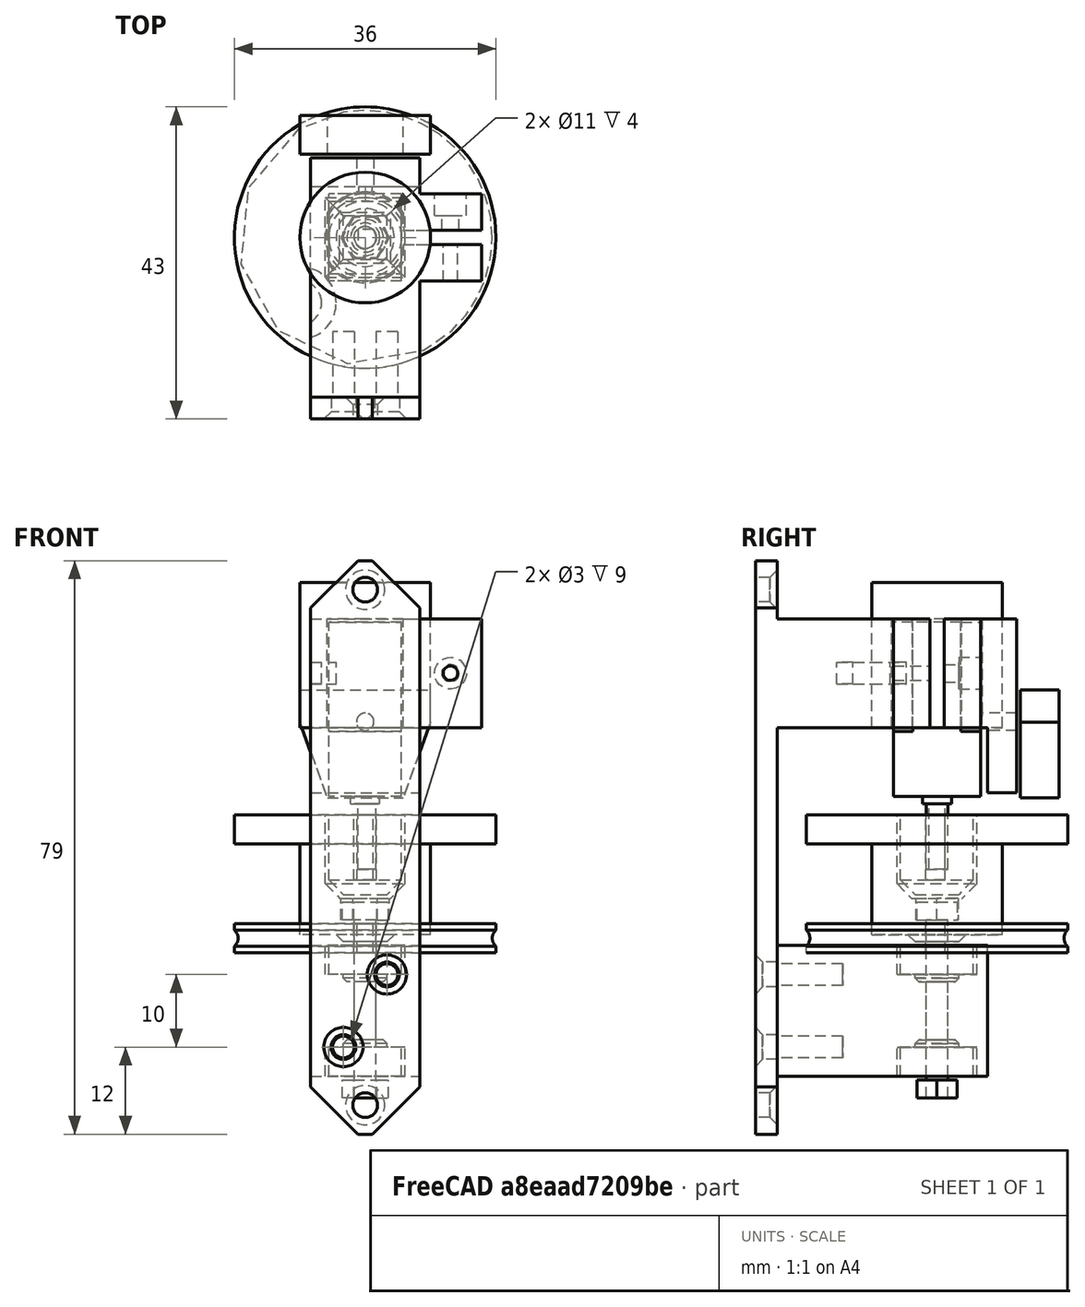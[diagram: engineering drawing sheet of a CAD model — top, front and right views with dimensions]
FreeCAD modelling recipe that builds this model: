
FCSTD DOCUMENT  (FreeCAD 0.18R16146 (Git))
Label: Motor and Opto Sensor Mount
License: All rights reserved
LicenseURL: http://en.wikipedia.org/wiki/All_rights_reserved
objects: Part::Cylinder×31, Part::Cut×23, Part::Box×19, Part::MultiFuse×13, Part::Chamfer×7, Part::Feature×3, Part::Fuse×3, Part::MultiCommon×2, Part::Torus×1, Part::Mirroring×1, Part::Cone×1
note: 104 computed .brp shape members not serialized (recipe doc carries the construction recipe); baked Part::Feature solids carry a one-line shape summary decoded from their .brp

FEATURE [Part::Box] Box406008004  label="gearbox004"
  AttacherType = Attacher::AttachEngine3D
  Height = 9
  Length = 12
  Placement = pos=(-6,-5,0) rot=(0,0,1;0rad)
  Width = 10
FEATURE [Part::Cylinder] Cylinder076  label="boss002"
  Angle = 360
  AttacherType = Attacher::AttachEngine3D
  Height = 1
  Placement = pos=(0,0,-1) rot=(0,0,1;0rad)
  Radius = 2
FEATURE [Part::Cylinder] Cylinder077
  Angle = 360
  AttacherType = Attacher::AttachEngine3D
  Height = 15
  Placement = pos=(0,0,9) rot=(0,0,1;0rad)
  Radius = 6
FEATURE [Part::Box] Box406008005  label="gearbox005"
  AttacherType = Attacher::AttachEngine3D
  Height = 27
  Length = 16
  Placement = pos=(-8,-5,0) rot=(0,0,1;0rad)
  Width = 10
FEATURE [Part::MultiCommon] Common001  label="motor002"
  Shapes = -> [Cylinder077,Box406008005]
FEATURE [Part::Cylinder] Cylinder078  label="shaft-002"
  Angle = 360
  AttacherType = Attacher::AttachEngine3D
  Height = 10
  Placement = pos=(0,0,-10) rot=(0,0,1;0rad)
  Radius = 1.5
FEATURE [Part::Box] Box406008006  label="Cube341"
  AttacherType = Attacher::AttachEngine3D
  Height = 12
  Length = 10
  Placement = pos=(-5,1,-11) rot=(0,0,1;0rad)
  Width = 10
FEATURE [Part::Cut] Cut001  label="shaft002"
  Base = -> Cylinder078
  Tool = -> Box406008006
FEATURE [Part::MultiFuse] Fusion103077013004017004  label="motor-assembled"
  Placement = pos=(0,0,20.5) rot=(0,0,1;1.5708rad)
  Shapes = -> [Box406008004,Cylinder076,Common001,Cut001]
FEATURE [Part::Cylinder] Cylinder028  label="Cylinder024"
  Angle = 360
  AttacherType = Attacher::AttachEngine3D
  Height = 10
  Placement = pos=(0,0,-1) rot=(0,0,1;0rad)
  Radius = 1.57
FEATURE [Part::Cylinder] Cylinder012  label="wheel1a"
  Angle = 360
  AttacherType = Attacher::AttachEngine3D
  Height = 4
  Radius = 18
FEATURE [Part::Box] Box084016  label="Cube067"
  AttacherType = Attacher::AttachEngine3D
  Height = 12
  Length = 10
  Placement = pos=(-5,1.1,-1.5) rot=(0,0,1;0rad)
  Width = 10
FEATURE [Part::Torus] Torus002
  Angle1 = -180
  Angle2 = 180
  Angle3 = 360
  AttacherType = Attacher::AttachEngine3D
  Placement = pos=(0,0,2) rot=(0,0,1;0rad)
  Radius1 = 19
  Radius2 = 1.5
FEATURE [Part::Cut] Cut057
  Base = -> Cylinder028
  Tool = -> Box084016
FEATURE [Part::Cut] Cut062
  Base = -> Cylinder012
  Tool = -> Cut057
FEATURE [Part::Cut] Cut063  label="wheel 0.1"
  Base = -> Cut062
  Placement = pos=(0,0,-1) rot=(0,0,1;0rad)
  Tool = -> Torus002
FEATURE [Part::Cylinder] Cylinder073  label="motor-bulge"
  Angle = 360
  AttacherType = Attacher::AttachEngine3D
  Height = 20
  Placement = pos=(0,0,30) rot=(0,0,1;0rad)
  Radius = 9
FEATURE [Part::Cylinder] Cylinder067
  Angle = 360
  AttacherType = Attacher::AttachEngine3D
  Height = 26
  Placement = pos=(0,0,20) rot=(0,0,1;0rad)
  Radius = 6.25
FEATURE [Part::Box] Box406017  label="gearbox001"
  AttacherType = Attacher::AttachEngine3D
  Height = 28
  Length = 16
  Placement = pos=(-8,-5.25,18) rot=(0,0,1;0rad)
  Width = 10.5
FEATURE [Part::MultiCommon] Common004  label="motor-hole"
  Placement = pos=(0,0,5) rot=(0,0,1;1.5708rad)
  Shapes = -> [Cylinder067,Box406017]
FEATURE [Part::Box] Box406016  label="clamp-slot"
  AttacherType = Attacher::AttachEngine3D
  Height = 32
  Length = 49
  Placement = pos=(48.48,1,22) rot=(0,0,1;3.14159rad)
  Width = 2
FEATURE [Part::Box] Box  label="Cube"
  AttacherType = Attacher::AttachEngine3D
  Height = 8
  Length = 15
  Placement = pos=(-7.5,-25,45) rot=(0,0,1;0rad)
  Width = 3
FEATURE [Part::Box] Box406008007  label="Cube342"
  AttacherType = Attacher::AttachEngine3D
  Height = 14.9
  Length = 18
  Placement = pos=(-9,13,34.3) rot=(0,0,1;0rad)
  Width = 5.3
FEATURE [Part::Cylinder] Cylinder079  label="Cylinder078"
  Angle = 360
  AttacherType = Attacher::AttachEngine3D
  Height = 17
  Placement = pos=(0,0,9) rot=(0,0,1;0rad)
  Radius = 1.57
FEATURE [Part::Box] Box406008008  label="Cube343"
  AttacherType = Attacher::AttachEngine3D
  Height = 19
  Length = 10
  Placement = pos=(-5,1.1,1.5) rot=(0,0,1;0rad)
  Width = 10
FEATURE [Part::Cut] Cut064  label="Motor Shaft Hole"
  Base = -> Cylinder079
  Tool = -> Box406008008
FEATURE [Part::Box] Box406008009  label="Cube344"
  AttacherType = Attacher::AttachEngine3D
  Height = 11
  Length = 10
  Placement = pos=(-5,-5,7) rot=(0,0,1;0rad)
  Width = 10
FEATURE [Part::Box] Box406008010  label="Cube345"
  AttacherType = Attacher::AttachEngine3D
  Height = 19.7
  Length = 17.5
  Placement = pos=(3.75,6,30.3) rot=(0,1,0;0.349066rad)
  Width = 13.3
FEATURE [Part::Box] Box406008011  label="Cube346"
  AttacherType = Attacher::AttachEngine3D
  Height = 19.7
  Length = 17.5
  Placement = pos=(3.75,6,30.3) rot=(0,1,0;0.349066rad)
  Width = 13.3
FEATURE [Part::Mirroring] Part__Mirroring  label="Cube346 (Mirror #1)"
  Base = (0,0,0)
  Normal = (1,0,0)
  Source = -> Box406008011
FEATURE [Part::MultiFuse] Fusion
  Shapes = -> [Box406008010,Part__Mirroring]
FEATURE [Part::Cut] Cut  label="Opto Sensor"
  Base = -> Box406008007
  Placement = pos=(0,-1.5,-14) rot=(0,0,1;0rad)
  Tool = -> Fusion
FEATURE [Part::Cut] Cut065  label="Square Peg"
  Base = -> Box406008009
  Tool = -> Cut064
FEATURE [Part::Box] Box406008012  label="Cube347"
  AttacherType = Attacher::AttachEngine3D
  Height = 11.5
  Length = 11
  Placement = pos=(-5.5,-5.5,6.5) rot=(0,0,1;0rad)
  Width = 11
FEATURE [Part::Cylinder] Cylinder
  Angle = 360
  AttacherType = Attacher::AttachEngine3D
  Height = 12.5
  Placement = pos=(0,0,1.5) rot=(0,0,1;0rad)
  Radius = 9
FEATURE [Part::Cylinder] Cylinder080  label="wheel1a001"
  Angle = 360
  AttacherType = Attacher::AttachEngine3D
  Height = 4
  Placement = pos=(0,0,14) rot=(0,0,1;0rad)
  Radius = 18
FEATURE [Part::Feature] Shape
  Placement = pos=(0,0,3.5) rot=(0,0,1;0rad)
  shape: bbox 6.697 x 5.8 x 15 mm, 8 faces (baked)
FEATURE [Part::MultiFuse] Fusion103077013004017005
  Shapes = -> [Cylinder080,Cylinder]
FEATURE [Part::Feature] Shape001
  Placement = pos=(0,0,3.5) rot=(0,0,1;0rad)
  shape: bbox 6.351 x 5.5 x 2.5 mm, 8 faces (baked)
FEATURE [Part::Cylinder] Cylinder081  label="Cylinder079"
  Angle = 360
  AttacherType = Attacher::AttachEngine3D
  Height = 25
  Placement = pos=(0,0,-21) rot=(0,0,1;0rad)
  Radius = 1.5
FEATURE [Part::MultiFuse] Fusion103077013004017006  label="M3 x 25 Hex Head"
  Shapes = -> [Shape001,Cylinder081]
FEATURE [Part::Cut] Cut066
  Base = -> Fusion103077013004017005
  Tool = -> Box406008012
FEATURE [Part::Cone] Cone
  Angle = 360
  AttacherType = Attacher::AttachEngine3D
  Height = 1
  Placement = pos=(0,0,0.5) rot=(0,0,1;0rad)
  Radius1 = 3
  Radius2 = 4
FEATURE [Part::MultiFuse] Fusion103077013004017007
  Shapes = -> [Cut066,Cone]
FEATURE [Part::Cut] Cut067
  Base = -> Fusion103077013004017007
  Tool = -> Shape
FEATURE [Part::Cylinder] Cylinder082  label="623 Bearing"
  Angle = 360
  AttacherType = Attacher::AttachEngine3D
  Height = 4
  Placement = pos=(0,0,-4) rot=(0,0,1;0rad)
  Radius = 5
FEATURE [Part::Cylinder] Cylinder083  label="623 Bearing001"
  Angle = 360
  AttacherType = Attacher::AttachEngine3D
  Height = 4
  Placement = pos=(0,0,-18) rot=(0,0,1;0rad)
  Radius = 5
FEATURE [Part::Feature] Shape002  label="Nylock"
  Placement = pos=(0,0,-21) rot=(0,0,1;0rad)
  shape: bbox 6.351 x 5.5 x 2.5 mm, 8 faces (baked)
FEATURE [Part::Cylinder] Cylinder084  label="Cylinder080"
  Angle = 360
  AttacherType = Attacher::AttachEngine3D
  Height = 6
  Placement = pos=(0,0,-2) rot=(0,0,1;0rad)
  Radius = 1.5
FEATURE [Part::Cut] Cut069
  Base = -> Cut067
  Tool = -> Cylinder084
FEATURE [Part::Cylinder] Cylinder085  label="Cylinder081"
  Angle = 360
  AttacherType = Attacher::AttachEngine3D
  Height = 12
  Placement = pos=(0,0,-14) rot=(0,0,1;0rad)
  Radius = 1.5
FEATURE [Part::Box] Box406008013  label="Cube348"
  AttacherType = Attacher::AttachEngine3D
  Height = 18
  Length = 15
  Placement = pos=(-7.5,-22,-18) rot=(0,0,1;0rad)
  Width = 29
FEATURE [Part::Cylinder] Cylinder086  label="623 Bearing002"
  Angle = 360
  AttacherType = Attacher::AttachEngine3D
  Height = 4
  Placement = pos=(0,0,-4) rot=(0,0,1;0rad)
  Radius = 5.5
FEATURE [Part::Cylinder] Cylinder087  label="623 Bearing003"
  Angle = 360
  AttacherType = Attacher::AttachEngine3D
  Height = 4
  Placement = pos=(0,0,-18) rot=(0,0,1;0rad)
  Radius = 5.5
FEATURE [Part::MultiFuse] Fusion103077013004017008  label="623 Bearing Holes"
  Shapes = -> [Cylinder086,Cylinder087]
FEATURE [Part::Cut] Cut070
  Base = -> Box406008013
  Tool = -> Fusion103077013004017008
FEATURE [Part::Cylinder] Cylinder088  label="Cylinder082"
  Angle = 360
  AttacherType = Attacher::AttachEngine3D
  Height = 1
  Placement = pos=(0,0,-5) rot=(0,0,1;0rad)
  Radius = 3
FEATURE [Part::Cylinder] Cylinder089  label="Cylinder083"
  Angle = 360
  AttacherType = Attacher::AttachEngine3D
  Height = 1
  Placement = pos=(0,0,-14) rot=(0,0,1;0rad)
  Radius = 3
FEATURE [Part::MultiFuse] Fusion103077013004017009
  Shapes = -> [Cylinder089,Cylinder088]
FEATURE [Part::Cut] Cut071
  Base = -> Cut070
  Tool = -> Fusion103077013004017009
FEATURE [Part::Cut] Cut072
  Base = -> Cut071
  Tool = -> Cylinder085
FEATURE [Part::Chamfer] Chamfer
  Base = -> Cut072
  Edges = 1 edges r=0.5: [Edge22]
FEATURE [Part::Chamfer] Chamfer001  label="Bearing Mount end"
  Base = -> Chamfer
  Edges = 1 edges r=0.5: [Edge16]
FEATURE [Part::Box] Box406008014  label="Cube349"
  AttacherType = Attacher::AttachEngine3D
  Height = 63
  Length = 15
  Placement = pos=(-7.5,-25,-18) rot=(0,0,1;0rad)
  Width = 3
FEATURE [Part::Box] Box406008015  label="Cube350"
  AttacherType = Attacher::AttachEngine3D
  Height = 15
  Length = 15
  Placement = pos=(-7.5,-22,35) rot=(0,0,1;0rad)
  Width = 31
FEATURE [Part::Cut] Cut073
  Base = -> Box406008015
  Tool = -> Common004
FEATURE [Part::Cylinder] Cylinder068
  Angle = 360
  AttacherType = Attacher::AttachEngine3D
  Height = 12
  Placement = pos=(11.75,0,42.5) rot=(0,0.707106,0.707107;3.14159rad)
  Radius = 1.2
FEATURE [Part::Cylinder] Cylinder069
  Angle = 360
  AttacherType = Attacher::AttachEngine3D
  Height = 12
  Placement = pos=(11.75,3,42.5) rot=(0,0.707106,0.707107;3.14159rad)
  Radius = 2.2
FEATURE [Part::MultiFuse] Fusion103077013  label="M2-screw001"
  Shapes = -> [Cylinder068,Cylinder069]
FEATURE [Part::Box] Box406008016  label="Cube351"
  AttacherType = Attacher::AttachEngine3D
  Height = 15
  Length = 9
  Placement = pos=(7,-6,35) rot=(0,0,1;0rad)
  Width = 12
FEATURE [Part::Fuse] Fusion103077013004017010
  Base = -> Cut073
  Tool = -> Box406008016
FEATURE [Part::Cut] Cut074
  Base = -> Fusion103077013004017010
  Tool = -> Box406016
FEATURE [Part::Box] Box406008017  label="Cube352"
  AttacherType = Attacher::AttachEngine3D
  Height = 24
  Length = 15
  Placement = pos=(-7.5,7,26) rot=(0,0,1;0rad)
  Width = 4
FEATURE [Part::Cylinder] Cylinder090  label="Cylinder084"
  Angle = 360
  AttacherType = Attacher::AttachEngine3D
  Height = 13
  Placement = pos=(0,16,35.8) rot=(1,0,0;1.5708rad)
  Radius = 1.2
FEATURE [Part::Cylinder] Cylinder091
  Angle = 360
  AttacherType = Attacher::AttachEngine3D
  Height = 12
  Placement = pos=(11.75,-12,42.5) rot=(0,0.707106,0.707107;3.14159rad)
  Radius = 1
FEATURE [Part::Fuse] Fusion103077013004017011
  Base = -> Fusion103077013
  Tool = -> Cylinder091
FEATURE [Part::Cut] Cut075
  Base = -> Cut074
  Tool = -> Fusion103077013004017011
FEATURE [Part::Fuse] Fusion103077013004017012
  Base = -> Box406008017
  Tool = -> Cut075
FEATURE [Part::Cut] Cut076  label="Motor Mount"
  Base = -> Fusion103077013004017012
  Placement = pos=(0,0,-5) rot=(0,0,1;0rad)
  Tool = -> Cylinder090
FEATURE [Part::Cylinder] Cylinder092
  Angle = 360
  AttacherType = Attacher::AttachEngine3D
  Height = 21
  Placement = pos=(-3,-13,-14) rot=(1,0,0;1.5708rad)
  Radius = 1.7
FEATURE [Part::Cylinder] Cylinder093
  Angle = 360
  AttacherType = Attacher::AttachEngine3D
  Height = 21
  Placement = pos=(3,-13,-4) rot=(1,0,0;1.5708rad)
  Radius = 1.7
FEATURE [Part::Cylinder] Cylinder094
  Angle = 360
  AttacherType = Attacher::AttachEngine3D
  Height = 21
  Placement = pos=(-3,-13,-14) rot=(1,0,0;1.5708rad)
  Radius = 1.5
FEATURE [Part::Cylinder] Cylinder095
  Angle = 360
  AttacherType = Attacher::AttachEngine3D
  Height = 21
  Placement = pos=(3,-13,-4) rot=(1,0,0;1.5708rad)
  Radius = 1.5
FEATURE [Part::MultiFuse] Fusion103077013004017013
  Shapes = -> [Cylinder092,Cylinder093]
FEATURE [Part::Cut] Cut077
  Base = -> Box406008014
  Tool = -> Fusion103077013004017013
FEATURE [Part::MultiFuse] Fusion103077013004017014
  Shapes = -> [Cylinder094,Cylinder095]
FEATURE [Part::Cut] Cut078  label="Bearing Mount End"
  Base = -> Chamfer001
  Tool = -> Fusion103077013004017014
FEATURE [Part::Cylinder] Cylinder096
  Angle = 360
  AttacherType = Attacher::AttachEngine3D
  Height = 21
  Placement = pos=(0,-13,49) rot=(1,0,0;1.5708rad)
  Radius = 1.7
FEATURE [Part::Cylinder] Cylinder097
  Angle = 360
  AttacherType = Attacher::AttachEngine3D
  Height = 21
  Placement = pos=(0,-13,-22) rot=(1,0,0;1.5708rad)
  Radius = 1.7
FEATURE [Part::Chamfer] Chamfer003  label="Wheel"
  Base = -> Cut069
  Edges = 4 edges r=2: [Edge11,Edge12,Edge15,Edge16]
FEATURE [Part::Chamfer] Chamfer004  label="Square Peg001"
  Base = -> Cut065
  Edges = 4 edges r=2: [Edge4,Edge5,Edge13,Edge15]
FEATURE [Part::Box] Box406008018  label="Cube353"
  AttacherType = Attacher::AttachEngine3D
  Height = 8
  Length = 15
  Placement = pos=(-7.5,-25,-26) rot=(0,0,1;0rad)
  Width = 3
FEATURE [Part::Cut] Cut079
  Base = -> Box406008018
  Tool = -> Cylinder097
FEATURE [Part::Cut] Cut080
  Base = -> Box
  Tool = -> Cylinder096
FEATURE [Part::MultiFuse] Fusion103077013004017015
  Shapes = -> [Cut079,Cut080]
FEATURE [Part::Chamfer] Chamfer005
  Base = -> Fusion103077013004017015
  Edges = 2 edges r=1: [Edge13,Edge28]
FEATURE [Part::Chamfer] Chamfer006
  Base = -> Cut077
  Edges = 2 edges r=1: [Edge8,Edge9]
FEATURE [Part::MultiFuse] Fusion103077013004017016
  Shapes = -> [Chamfer006,Chamfer005]
FEATURE [Part::Chamfer] Chamfer007
  Base = -> Fusion103077013004017016
  Edges = 4 edges r=6.5: [Edge27,Edge29,Edge34,Edge39]
FEATURE [Part::Cylinder] Cylinder098
  Angle = 360
  AttacherType = Attacher::AttachEngine3D
  Height = 3
  Placement = pos=(-9,-9,36) rot=(1,0,0;0rad)
  Radius = 5
FEATURE [Part::Cylinder] Cylinder099
  Angle = 360
  AttacherType = Attacher::AttachEngine3D
  Height = 3
  Placement = pos=(-9,-9,36) rot=(1,0,0;0rad)
  Radius = 3
FEATURE [Part::Cut] Cut081
  Base = -> Cylinder098
  Tool = -> Cylinder099
FEATURE [Part::Cut] Cut082
  Base = -> Cut076
  Tool = -> Cut081
FEATURE [Part::MultiFuse] Fusion103077013004017017
  Shapes = -> [Chamfer007,Cut082]
